AUTODESK INVENTOR PART (.ipt)
format: ipt  version: 2024 (Build 280153000, 153)  size: 235,520 bytes
history: native  units: in
note: dims shown in document units (in); Inventor stores cm internally (conversion verified against a paired STEP export)
features: extrude x1, sketch x1
ambient origin geometry x8: Origin, YZ Plane, XZ Plane, XY Plane, X Axis, Y Axis, Z Axis, Center Point
bodies: Solid1 (feature_tree)
feature tree (2):
  extrude  "Extrusion1"  Depth=0.6in
  sketch  "Sketch1"  dims[d0=3.0in d1=0.6in d2=2.36in d3=1.5in d4=2.8in d5=1.125in d6=0.813in d8=0.375in d9=2.9in d10=0.1in d12=0.5in d13=0.196in d14=0.0625in d15=0.5in d16=0.196in d17=0.5in d18=0.196in d19=0.5in d20=0.196in d21=0.0625in d22=0.0625in d23=0.0625in d24=0.0625in d25=0.1875in d26=0.0in d27=0.159in d28=0.159in d29=6.0in d30=0.375in]
